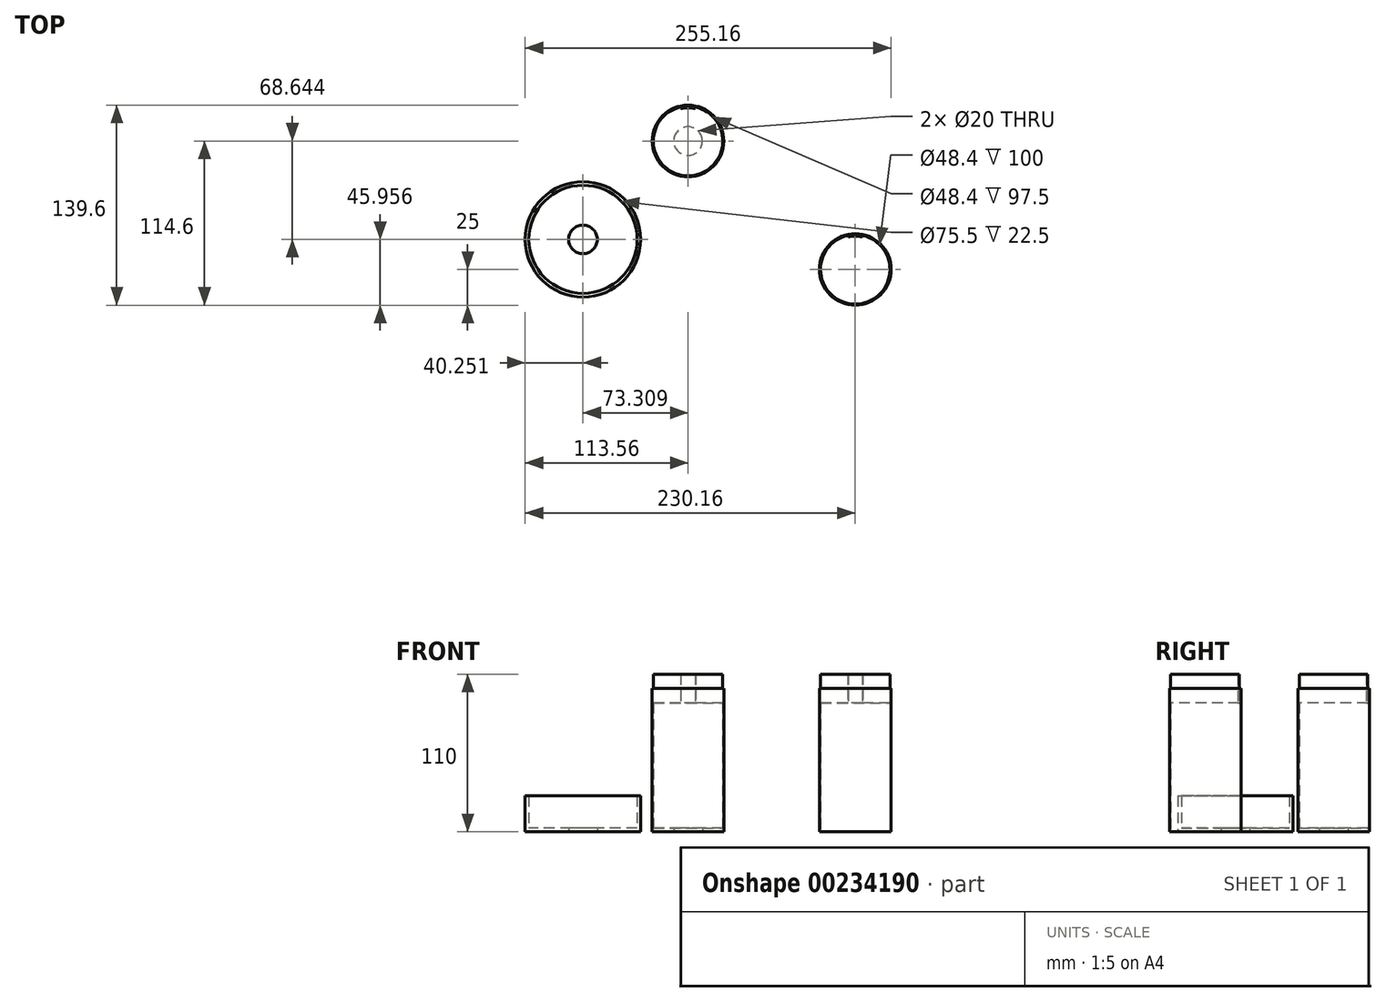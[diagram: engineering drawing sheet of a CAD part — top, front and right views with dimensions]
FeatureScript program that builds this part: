
annotation { "Feature Type Name" : "Feature", "Feature Type Description" : "" }
export const myFeature = defineFeature(function(context is Context, id is Id, definition is map)
    precondition{}
    {
        {
            assignVariable(context, id + "F0", {"name" : "height", "anyValue" : 100});
        }
        {
            assignVariable(context, id + "F1", {"name" : "thickness", "anyValue" : 0.8});
        }
        {
            assignVariable(context, id + "F2", {"name" : "basethickness", "anyValue" : 2.5});
        }
        {
            assignVariable(context, id + "F3", {"name" : "baseheight", "anyValue" : 25});
        }
        {
            var Q0;
            Q0=qCreatedBy(makeId("Top.planeOp"),FACE);
            var sketch = newSketch(context, id + "F4", { "sketchPlane" : qUnion([Q0])});
            skCircle(sketch, "E0", {"center": v(0, 0) * mm, "radius": 25 * mm});
            skCircle(sketch, "E1", {"center": v(0, 0) * mm, "radius": 24.2 * mm});
            skCircle(sketch, "E2", {"center": v(0, 0) * mm, "radius": 10 * mm});
            skSolve(sketch);
        }
        {
            var Q0;
            Q0 = qSketchRegion(id + "F4", true);
            extrude(context, id + "F5", {"entities" : qUnion([Q0]), "depth" : (getVariable(context, 'thickness')) * mm});
        }
        {
            var Q0;
            Q0=makeQuery(id+"F4.imprint","IMPRINT",FACE,{"disambiguationData":[TD([[makeQuery(id+"F4.imprint","IMPRINT",EDGE,{"derivedFrom":sQuery(id+"F4.wireOp",EDGE,"E0")}),1.0]])]});
            extrude(context, id + "F6", {"entities" : qUnion([Q0]), "operationType" : NewBodyOperationType.ADD, "depth" : (getVariable(context, 'height')) * mm});
        }
        {
            var Q0;
            Q0=makeQuery(id+"F6.opExtrude","CAP_FACE",FACE,{"disambiguationData":[OSD([sQuery(id+"F4.wireOp",EDGE,"E0"),sQuery(id+"F4.wireOp",EDGE,"E1")])],"isStart":false});
            var sketch = newSketch(context, id + "F7", { "sketchPlane" : qUnion([Q0])});
            skArc(sketch, "E3", {"start": v(-5, 22.65) * mm, "mid": v(-2.51, 23.06) * mm, "end": v(0, 23.2) * mm});
            skLineSegment(sketch, "E4", {"start": v(0, 0) * mm, "end": v(-5, 22.65) * mm, "construction": true});
            skLineSegment(sketch, "E5", {"start": v(-5, 22.65) * mm, "end": v(-5.22, 23.63) * mm});
            skArc(sketch, "E6", {"start": v(-5.22, 23.63) * mm, "mid": v(-2.62, 24.06) * mm, "end": v(0, 24.2) * mm});
            skArc(sketch, "E7.MirrorCS", {"start": v(5, 22.65) * mm, "mid": v(2.51, 23.06) * mm, "end": v(0, 23.2) * mm});
            skArc(sketch, "E8.MirrorCS", {"start": v(5.22, 23.63) * mm, "mid": v(2.62, 24.06) * mm, "end": v(0, 24.2) * mm});
            skLineSegment(sketch, "E9.MirrorCS", {"start": v(5, 22.65) * mm, "end": v(5.22, 23.63) * mm});
            skLineSegment(sketch, "E10", {"start": v(0, 0) * mm, "end": v(5, 22.65) * mm, "construction": true});
            skArc(sketch, "E11.1.0", {"start": v(-20.86, 12.26) * mm, "mid": v(-22.07, 9.93) * mm, "end": v(-23.02, 7.48) * mm});
            skLineSegment(sketch, "E11.1.1", {"start": v(0, 0) * mm, "end": v(-23.1, 2.25) * mm, "construction": true});
            skArc(sketch, "E11.1.2", {"start": v(-20, 11.76) * mm, "mid": v(-21.16, 9.52) * mm, "end": v(-22.06, 7.17) * mm});
            skArc(sketch, "E11.1.3", {"start": v(-24.09, 2.34) * mm, "mid": v(-23.7, 4.94) * mm, "end": v(-23.02, 7.48) * mm});
            skArc(sketch, "E11.1.4", {"start": v(-23.1, 2.25) * mm, "mid": v(-22.71, 4.74) * mm, "end": v(-22.06, 7.17) * mm});
            skLineSegment(sketch, "E11.1.5", {"start": v(-23.1, 2.25) * mm, "end": v(-24.09, 2.34) * mm});
            skLineSegment(sketch, "E11.1.6", {"start": v(-20, 11.76) * mm, "end": v(-20.86, 12.26) * mm});
            skLineSegment(sketch, "E11.1.7", {"start": v(0, 0) * mm, "end": v(-20, 11.76) * mm, "construction": true});
            skArc(sketch, "E11.2.0", {"start": v(-18.1, -16.05) * mm, "mid": v(-16.26, -17.92) * mm, "end": v(-14.22, -19.58) * mm});
            skLineSegment(sketch, "E11.2.1", {"start": v(0, 0) * mm, "end": v(-9.27, -21.27) * mm, "construction": true});
            skArc(sketch, "E11.2.2", {"start": v(-17.36, -15.39) * mm, "mid": v(-15.6, -17.18) * mm, "end": v(-13.64, -18.77) * mm});
            skArc(sketch, "E11.2.3", {"start": v(-9.67, -22.18) * mm, "mid": v(-12.02, -21) * mm, "end": v(-14.22, -19.58) * mm});
            skArc(sketch, "E11.2.4", {"start": v(-9.27, -21.27) * mm, "mid": v(-11.52, -20.14) * mm, "end": v(-13.64, -18.77) * mm});
            skLineSegment(sketch, "E11.2.5", {"start": v(-9.27, -21.27) * mm, "end": v(-9.67, -22.18) * mm});
            skLineSegment(sketch, "E11.2.6", {"start": v(-17.36, -15.39) * mm, "end": v(-18.1, -16.05) * mm});
            skLineSegment(sketch, "E11.2.7", {"start": v(0, 0) * mm, "end": v(-17.36, -15.39) * mm, "construction": true});
            skArc(sketch, "E11.3.0", {"start": v(9.67, -22.18) * mm, "mid": v(12.02, -21) * mm, "end": v(14.22, -19.58) * mm});
            skLineSegment(sketch, "E11.3.1", {"start": v(0, 0) * mm, "end": v(17.36, -15.39) * mm, "construction": true});
            skArc(sketch, "E11.3.2", {"start": v(9.27, -21.27) * mm, "mid": v(11.52, -20.14) * mm, "end": v(13.64, -18.77) * mm});
            skArc(sketch, "E11.3.3", {"start": v(18.1, -16.05) * mm, "mid": v(16.26, -17.92) * mm, "end": v(14.22, -19.58) * mm});
            skArc(sketch, "E11.3.4", {"start": v(17.36, -15.39) * mm, "mid": v(15.6, -17.18) * mm, "end": v(13.64, -18.77) * mm});
            skLineSegment(sketch, "E11.3.5", {"start": v(17.36, -15.39) * mm, "end": v(18.1, -16.05) * mm});
            skLineSegment(sketch, "E11.3.6", {"start": v(9.27, -21.27) * mm, "end": v(9.67, -22.18) * mm});
            skLineSegment(sketch, "E11.3.7", {"start": v(0, 0) * mm, "end": v(9.27, -21.27) * mm, "construction": true});
            skArc(sketch, "E11.4.0", {"start": v(24.09, 2.34) * mm, "mid": v(23.7, 4.94) * mm, "end": v(23.02, 7.48) * mm});
            skLineSegment(sketch, "E11.4.1", {"start": v(0, 0) * mm, "end": v(20, 11.76) * mm, "construction": true});
            skArc(sketch, "E11.4.2", {"start": v(23.1, 2.25) * mm, "mid": v(22.71, 4.74) * mm, "end": v(22.06, 7.17) * mm});
            skArc(sketch, "E11.4.3", {"start": v(20.86, 12.26) * mm, "mid": v(22.07, 9.93) * mm, "end": v(23.02, 7.48) * mm});
            skArc(sketch, "E11.4.4", {"start": v(20, 11.76) * mm, "mid": v(21.16, 9.52) * mm, "end": v(22.06, 7.17) * mm});
            skLineSegment(sketch, "E11.4.5", {"start": v(20, 11.76) * mm, "end": v(20.86, 12.26) * mm});
            skLineSegment(sketch, "E11.4.6", {"start": v(23.1, 2.25) * mm, "end": v(24.09, 2.34) * mm});
            skLineSegment(sketch, "E11.4.7", {"start": v(0, 0) * mm, "end": v(23.1, 2.25) * mm, "construction": true});
            skSolve(sketch);
        }
        {
            var Q0;
            Q0=makeQuery(id+"F7.imprint","IMPRINT",FACE,{"disambiguationData":[TD([[makeQuery(id+"F7.imprint","IMPRINT",EDGE,{"derivedFrom":sQuery(id+"F7.wireOp",EDGE,"E11.2.0")}),1.0]])]});
            var Q1;
            Q1=makeQuery(id+"F7.imprint","IMPRINT",FACE,{"disambiguationData":[TD([[makeQuery(id+"F7.imprint","IMPRINT",EDGE,{"derivedFrom":sQuery(id+"F7.wireOp",EDGE,"E11.1.0")}),1.0]])]});
            var Q2;
            Q2=makeQuery(id+"F7.imprint","IMPRINT",FACE,{"disambiguationData":[TD([[makeQuery(id+"F7.imprint","IMPRINT",EDGE,{"derivedFrom":sQuery(id+"F7.wireOp",EDGE,"E3")}),1.0]])]});
            var Q3;
            Q3=makeQuery(id+"F7.imprint","IMPRINT",FACE,{"disambiguationData":[TD([[makeQuery(id+"F7.imprint","IMPRINT",EDGE,{"derivedFrom":sQuery(id+"F7.wireOp",EDGE,"E11.4.0")}),1.0]])]});
            var Q4;
            Q4=makeQuery(id+"F7.imprint","IMPRINT",FACE,{"disambiguationData":[TD([[makeQuery(id+"F7.imprint","IMPRINT",EDGE,{"derivedFrom":sQuery(id+"F7.wireOp",EDGE,"E11.3.0")}),1.0]])]});
            extrude(context, id + "F8", {"entities" : qUnion([Q0, Q1, Q2, Q3, Q4]), "operationType" : NewBodyOperationType.ADD, "depth" : 10 * mm, "hasSecondDirection" : true, "secondDirectionOppositeDirection" : true, "secondDirectionDepth" : 10 * mm});
        }
        {
            var Q0;
            Q0=makeQuery(id+"F5.opExtrude","SWEPT_BODY",BODY,{"disambiguationData":[OSD([sQuery(id+"F4.wireOp",EDGE,"E0"),sQuery(id+"F4.wireOp",EDGE,"E1")])]});
            transform(context, id + "F9", {"entities" : qUnion([Q0]), "transformType" : TransformType.TRANSLATION_3D, "dx" : 116.6 * mm, "dy" : -89.6 * mm, "dz" : 0 * mm, "makeCopy" : true});
        }
        {
            var Q0;
            Q0=makeQuery(id+"F4.imprint","IMPRINT",FACE,{"disambiguationData":[TD([[makeQuery(id+"F4.imprint","IMPRINT",EDGE,{"derivedFrom":sQuery(id+"F4.wireOp",EDGE,"E1")}),1.0]])]});
            extrude(context, id + "F10", {"entities" : qUnion([Q0]), "operationType" : NewBodyOperationType.ADD, "depth" : 2.5 * mm});
        }
        {
            var Q0;
            Q0=qCreatedBy(makeId("Top.planeOp"),FACE);
            var sketch = newSketch(context, id + "F11", { "sketchPlane" : qUnion([Q0])});
            skCircle(sketch, "E12", {"center": v(-73.3, -68.64) * mm, "radius": 40.25 * mm});
            skCircle(sketch, "E13", {"center": v(-73.3, -68.64) * mm, "radius": 10 * mm});
            skCircle(sketch, "E14", {"center": v(-73.3, -68.64) * mm, "radius": 37.75 * mm});
            skSolve(sketch);
        }
        {
            var Q0;
            Q0=makeQuery(id+"F11.imprint","IMPRINT",FACE,{"disambiguationData":[TD([[makeQuery(id+"F11.imprint","IMPRINT",EDGE,{"derivedFrom":sQuery(id+"F11.wireOp",EDGE,"E13")}),-1.0]])]});
            var Q1;
            Q1=makeQuery(id+"F11.imprint","IMPRINT",FACE,{"disambiguationData":[TD([[makeQuery(id+"F11.imprint","IMPRINT",EDGE,{"derivedFrom":sQuery(id+"F11.wireOp",EDGE,"E12")}),1.0]])]});
            extrude(context, id + "F12", {"entities" : qUnion([Q0, Q1]), "depth" : (getVariable(context, 'basethickness')) * mm});
        }
        {
            var Q0;
            Q0=makeQuery(id+"F11.imprint","IMPRINT",FACE,{"disambiguationData":[TD([[makeQuery(id+"F11.imprint","IMPRINT",EDGE,{"derivedFrom":sQuery(id+"F11.wireOp",EDGE,"E12")}),1.0]])]});
            extrude(context, id + "F13", {"entities" : qUnion([Q0]), "operationType" : NewBodyOperationType.ADD, "depth" : (getVariable(context, 'baseheight')) * mm});
        }
    });
